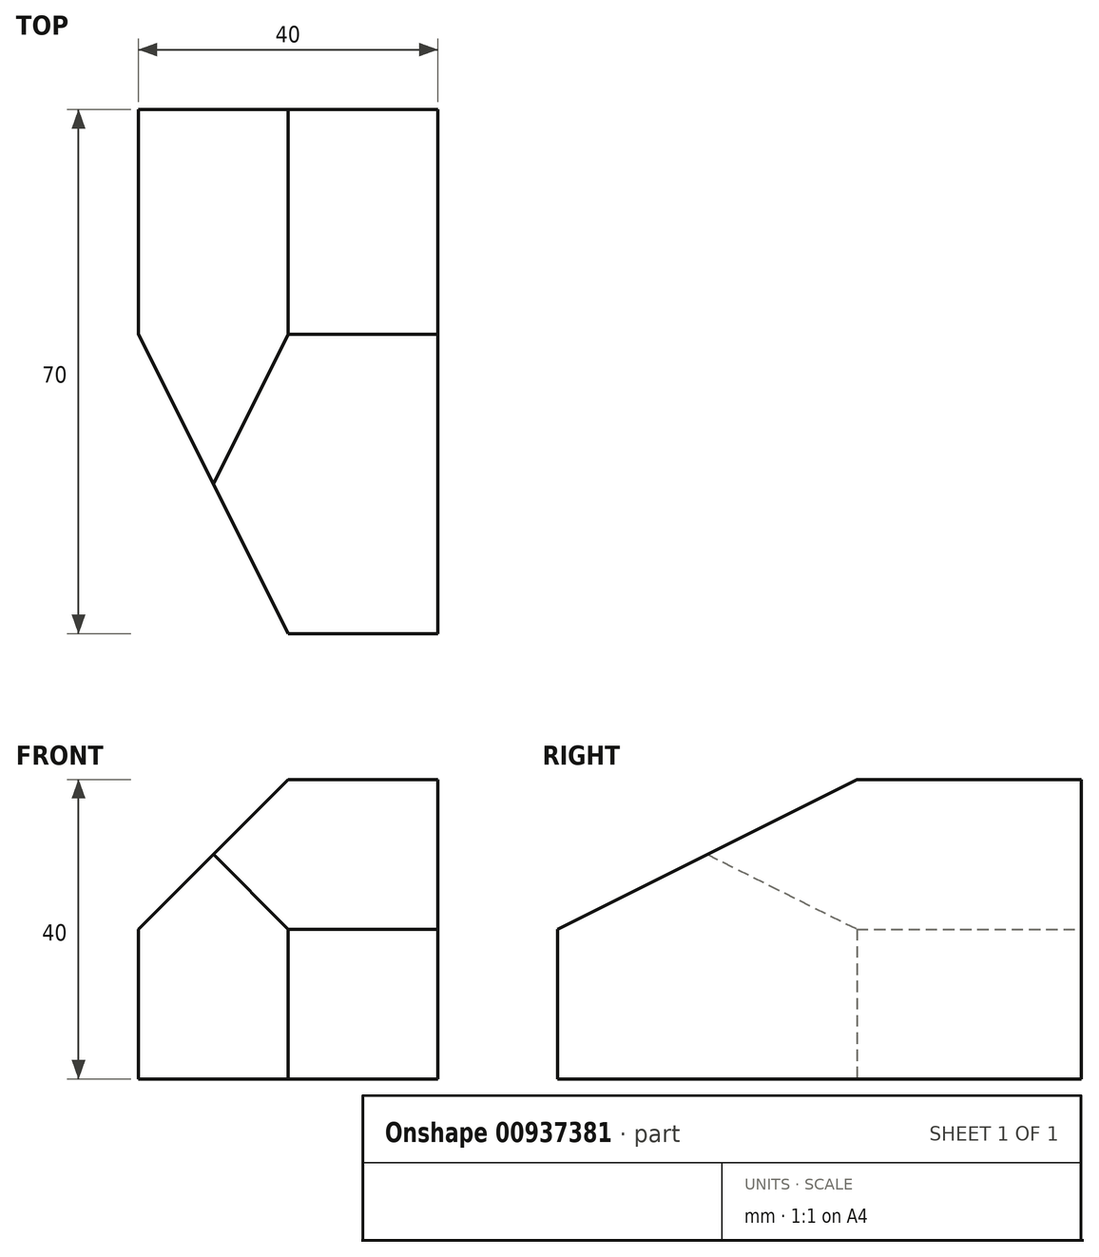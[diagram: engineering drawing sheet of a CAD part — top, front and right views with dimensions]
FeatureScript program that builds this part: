
annotation { "Feature Type Name" : "Feature", "Feature Type Description" : "" }
export const myFeature = defineFeature(function(context is Context, id is Id, definition is map)
    precondition{}
    {
        {
            var Q0;
            Q0=qCreatedBy(makeId("Front.planeOp"),FACE);
            var sketch = newSketch(context, id + "F0", { "sketchPlane" : qUnion([Q0])});
            skLineSegment(sketch, "E0.bottom", {"start": v(0, 0) * mm, "end": v(40, 0) * mm});
            skLineSegment(sketch, "E0.top", {"start": v(20, 40) * mm, "end": v(40, 40) * mm});
            skLineSegment(sketch, "E0.left", {"start": v(0, 0) * mm, "end": v(0, 20) * mm});
            skLineSegment(sketch, "E0.right", {"start": v(40, 0) * mm, "end": v(40, 40) * mm});
            skLineSegment(sketch, "E1", {"start": v(0, 20) * mm, "end": v(20, 40) * mm});
            skPoint(sketch, "E2.orphan", {"position": v(0, 40) * mm});
            skSolve(sketch);
        }
        {
            var Q0;
            Q0=makeQuery(id+"F0.imprint","IMPRINT",FACE,{"disambiguationData":[TD([[makeQuery(id+"F0.imprint","IMPRINT",EDGE,{"derivedFrom":sQuery(id+"F0.wireOp",EDGE,"E0.bottom")}),1.0]])]});
            extrude(context, id + "F1", {"entities" : qUnion([Q0]), "depth" : 70 * mm, "offsetDistance" : 25 * mm});
        }
        {
            var Q0;
            Q0=makeQuery(id+"F1.opExtrude","SWEPT_FACE",FACE,{"disambiguationData":[OSD([sQuery(id+"F0.wireOp",EDGE,"E0.bottom")])]});
            var sketch = newSketch(context, id + "F2", { "sketchPlane" : qUnion([Q0])});
            skLineSegment(sketch, "E3.0.2", {"start": v(20, 70) * mm, "end": v(0, 70) * mm});
            skLineSegment(sketch, "E3.0.3", {"start": v(0, 70) * mm, "end": v(0, 30) * mm});
            skLineSegment(sketch, "E4", {"start": v(0, 30) * mm, "end": v(20, 70) * mm});
            skPoint(sketch, "E3.0.0.start.orphan", {"position": v(0, 0) * mm});
            skPoint(sketch, "E3.0.1.end.orphan", {"position": v(40, 70) * mm});
            skPoint(sketch, "E3.0.1.start.orphan", {"position": v(40, 0) * mm});
            skSolve(sketch);
        }
        {
            var Q0;
            Q0=makeQuery(id+"F2.imprint","IMPRINT",FACE,{"disambiguationData":[TD([[makeQuery(id+"F2.imprint","IMPRINT",EDGE,{"derivedFrom":sQuery(id+"F2.wireOp",EDGE,"E3.0.2")}),-1.0]])]});
            extrude(context, id + "F3", {"entities" : qUnion([Q0]), "operationType" : NewBodyOperationType.REMOVE, "endBound" : BoundingType.THROUGH_ALL, "oppositeDirection" : true, "depth" : 25 * mm, "offsetDistance" : 25 * mm});
        }
        {
            var Q0;
            Q0=makeQuery(id+"F1.opExtrude","SWEPT_FACE",FACE,{"disambiguationData":[OSD([sQuery(id+"F0.wireOp",EDGE,"E0.right")])]});
            var sketch = newSketch(context, id + "F4", { "sketchPlane" : qUnion([Q0])});
            skLineSegment(sketch, "E5.0", {"start": v(-70, 20) * mm, "end": v(-70, 40) * mm});
            skLineSegment(sketch, "E5.1", {"start": v(-70, 40) * mm, "end": v(-30, 40) * mm});
            skLineSegment(sketch, "E6", {"start": v(-70, 20) * mm, "end": v(-30, 40) * mm});
            skPoint(sketch, "E7.orphan", {"position": v(0, 40) * mm});
            skPoint(sketch, "E8.orphan", {"position": v(-70, 0) * mm});
            skSolve(sketch);
        }
        {
            var Q0;
            Q0=makeQuery(id+"F4.imprint","IMPRINT",FACE,{"disambiguationData":[TD([[makeQuery(id+"F4.imprint","IMPRINT",EDGE,{"derivedFrom":sQuery(id+"F4.wireOp",EDGE,"E5.0")}),-1.0]])]});
            extrude(context, id + "F5", {"entities" : qUnion([Q0]), "operationType" : NewBodyOperationType.REMOVE, "endBound" : BoundingType.THROUGH_ALL, "oppositeDirection" : true, "depth" : 25 * mm, "offsetDistance" : 25 * mm});
        }
    });
